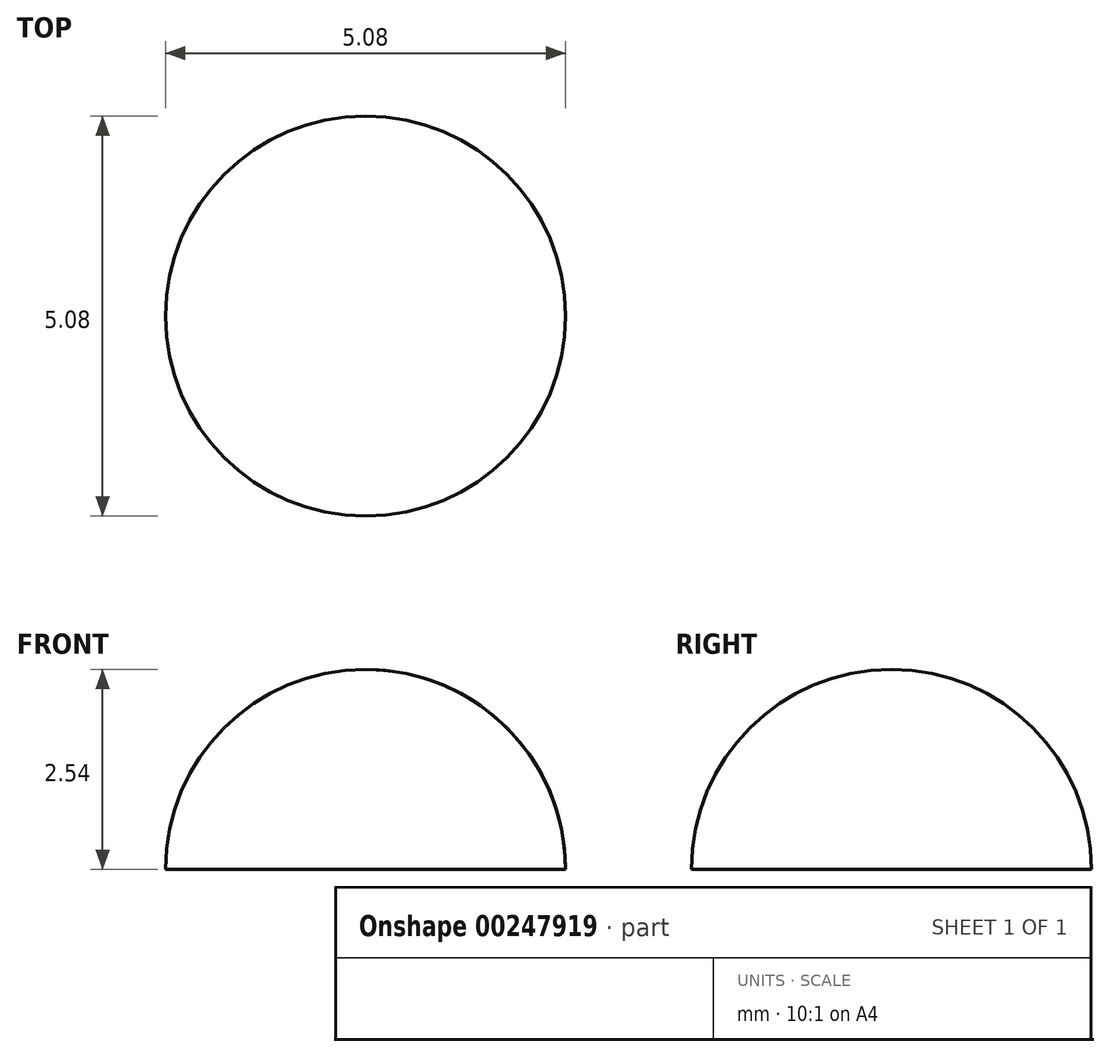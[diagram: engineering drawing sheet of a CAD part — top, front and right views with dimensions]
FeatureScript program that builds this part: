
annotation { "Feature Type Name" : "Feature", "Feature Type Description" : "" }
export const myFeature = defineFeature(function(context is Context, id is Id, definition is map)
    precondition{}
    {
        {
            var Q0;
            Q0=qCreatedBy(makeId("Front.planeOp"),FACE);
            var sketch = newSketch(context, id + "F0", { "sketchPlane" : qUnion([Q0])});
            skArc(sketch, "E0", {"start": v(0, 2.54) * mm, "mid": v(-1.8, 1.8) * mm, "end": v(-2.54, 0) * mm});
            skLineSegment(sketch, "E1", {"start": v(0, 0) * mm, "end": v(0, 2.54) * mm});
            skLineSegment(sketch, "E2", {"start": v(0, 0) * mm, "end": v(-2.54, 0) * mm});
            skSolve(sketch);
        }
        {
            var Q0;
            Q0=makeQuery(id+"F0.imprint","IMPRINT",FACE,{"disambiguationData":[TD([[makeQuery(id+"F0.imprint","IMPRINT",EDGE,{"derivedFrom":sQuery(id+"F0.wireOp",EDGE,"E0")}),1.0]])]});
            var Q1;
            Q1=sQuery(id+"F0.wireOp",EDGE,"E1");
            revolve(context, id + "F1", {"entities" : qUnion([Q0]), "axis" : qUnion([Q1]), "revolveType" : RevolveType.FULL});
        }
    });
